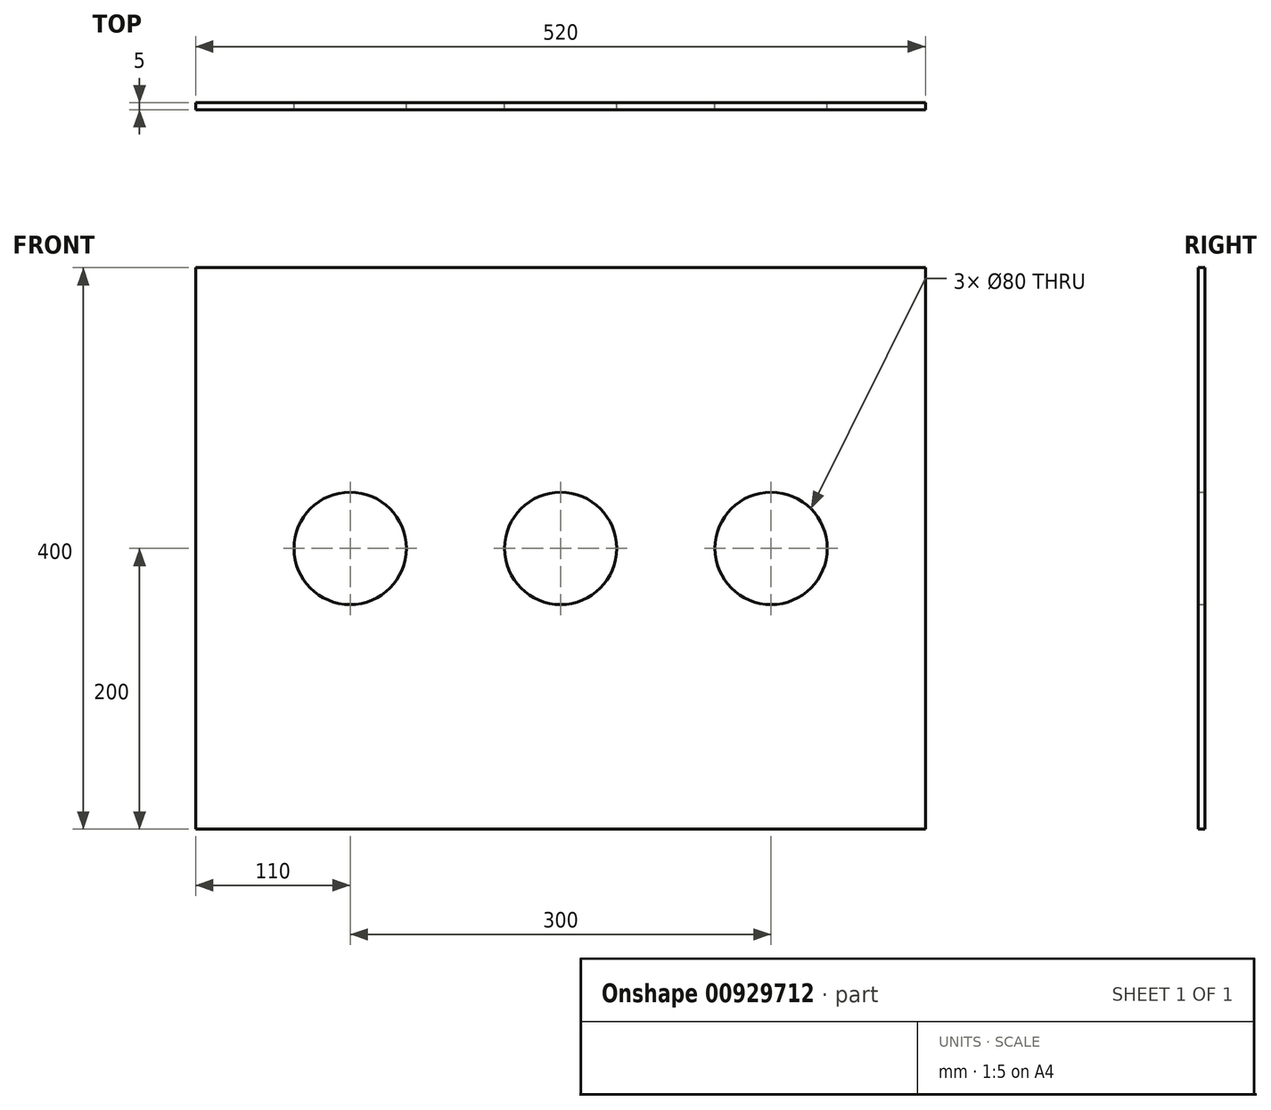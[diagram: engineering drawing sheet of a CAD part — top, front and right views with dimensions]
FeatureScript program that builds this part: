
annotation { "Feature Type Name" : "Feature", "Feature Type Description" : "" }
export const myFeature = defineFeature(function(context is Context, id is Id, definition is map)
    precondition{}
    {
        {
            var Q0;
            Q0=qCreatedBy(makeId("Front.planeOp"),FACE);
            var sketch = newSketch(context, id + "F0", { "sketchPlane" : qUnion([Q0])});
            skLineSegment(sketch, "E0.bottom", {"start": v(260, 200) * mm, "end": v(-260, 200) * mm});
            skLineSegment(sketch, "E0.top", {"start": v(260, -200) * mm, "end": v(-260, -200) * mm});
            skLineSegment(sketch, "E0.left", {"start": v(260, 200) * mm, "end": v(260, -200) * mm});
            skLineSegment(sketch, "E0.right", {"start": v(-260, 200) * mm, "end": v(-260, -200) * mm});
            skPoint(sketch, "E0.middle", {"position": v(0, 0) * mm});
            skLineSegment(sketch, "E1", {"start": v(-260, 0) * mm, "end": v(260, 0) * mm, "construction": true});
            skCircle(sketch, "E2", {"center": v(0, 0) * mm, "radius": 40 * mm});
            skCircle(sketch, "E3", {"center": v(-150, 0) * mm, "radius": 40 * mm});
            skCircle(sketch, "E4", {"center": v(150, 0) * mm, "radius": 40 * mm});
            skSolve(sketch);
        }
        {
            var Q0;
            Q0=makeQuery(id+"F0.imprint","IMPRINT",FACE,{"disambiguationData":[TD([[makeQuery(id+"F0.imprint","IMPRINT",EDGE,{"derivedFrom":sQuery(id+"F0.wireOp",EDGE,"E0.bottom")}),1.0]])]});
            extrude(context, id + "F1", {"entities" : qUnion([Q0]), "depth" : 5 * mm, "offsetDistance" : 25 * mm});
        }
    });
